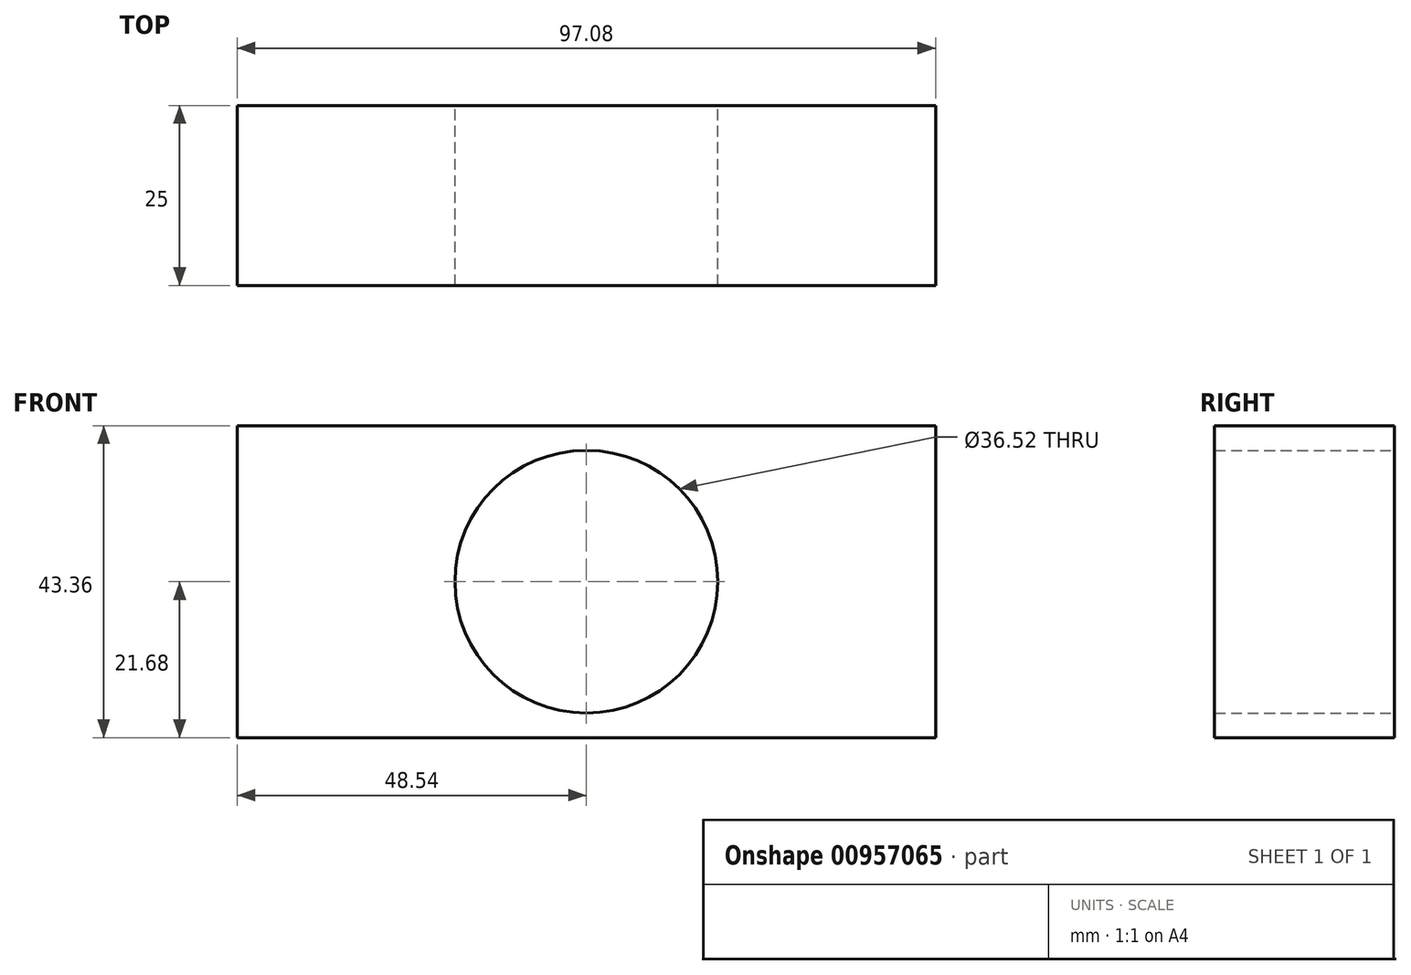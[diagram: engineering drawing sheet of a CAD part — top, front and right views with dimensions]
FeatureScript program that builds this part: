
annotation { "Feature Type Name" : "Feature", "Feature Type Description" : "" }
export const myFeature = defineFeature(function(context is Context, id is Id, definition is map)
    precondition{}
    {
        {
            var Q0;
            Q0=qCreatedBy(makeId("Front.planeOp"),FACE);
            var sketch = newSketch(context, id + "F0", { "sketchPlane" : qUnion([Q0])});
            skCircle(sketch, "E0", {"center": v(0, 0) * mm, "radius": 18.26 * mm});
            skLineSegment(sketch, "E1.bottom", {"start": v(48.54, 21.68) * mm, "end": v(-48.54, 21.68) * mm});
            skLineSegment(sketch, "E1.top", {"start": v(48.54, -21.68) * mm, "end": v(-48.54, -21.68) * mm});
            skLineSegment(sketch, "E1.left", {"start": v(48.54, 21.68) * mm, "end": v(48.54, -21.68) * mm});
            skLineSegment(sketch, "E1.right", {"start": v(-48.54, 21.68) * mm, "end": v(-48.54, -21.68) * mm});
            skSolve(sketch);
        }
        {
            var Q0;
            Q0 = qSketchRegion(id + "F0", true);
            extrude(context, id + "F1", {"entities" : qUnion([Q0]), "depth" : 25 * mm, "offsetDistance" : 25 * mm});
        }
    });
